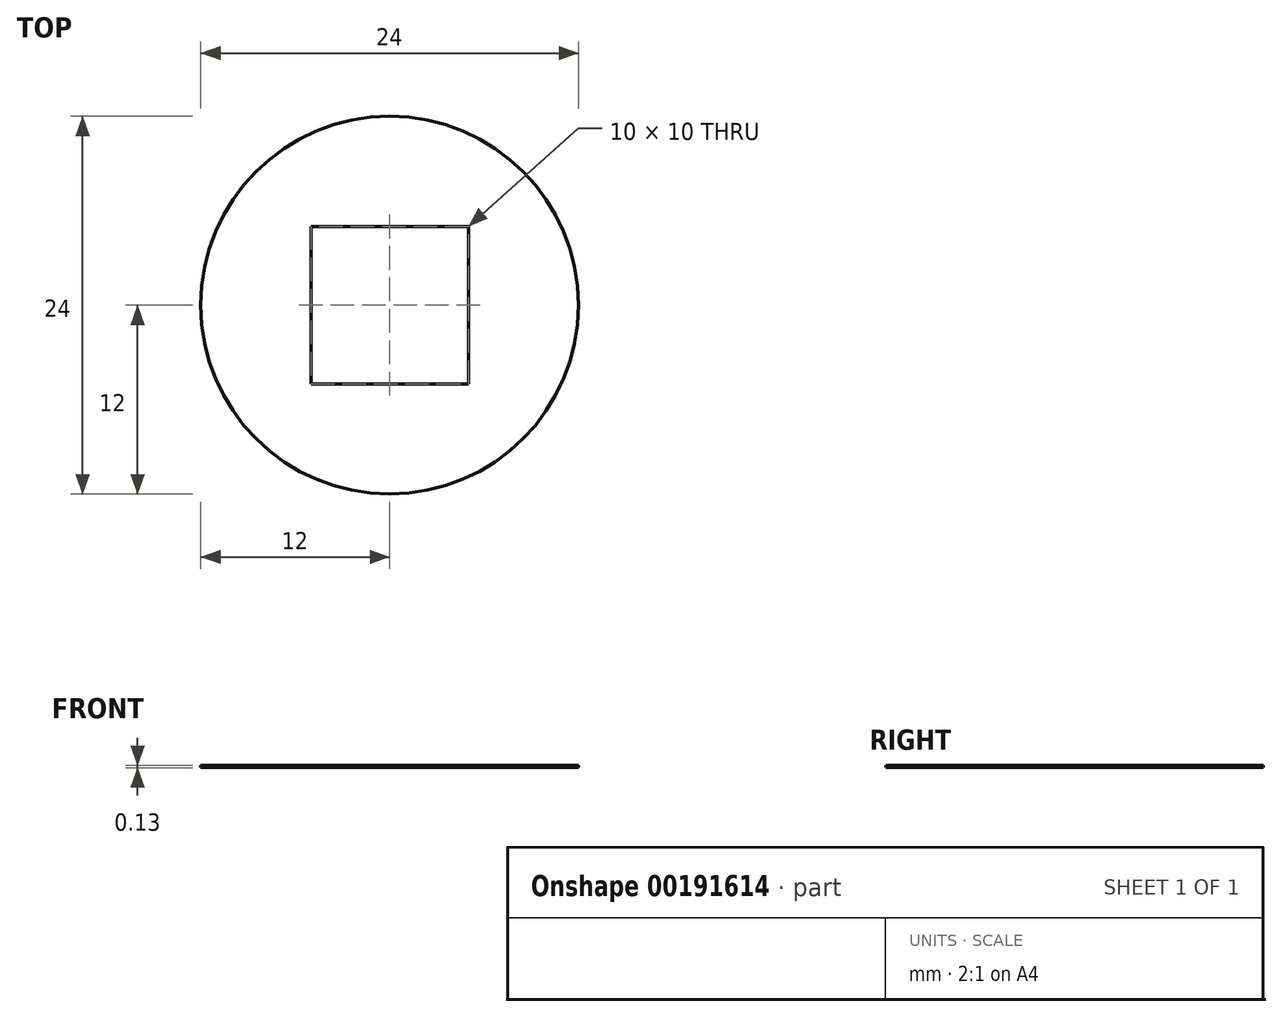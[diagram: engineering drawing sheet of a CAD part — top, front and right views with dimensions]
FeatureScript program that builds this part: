
annotation { "Feature Type Name" : "Feature", "Feature Type Description" : "" }
export const myFeature = defineFeature(function(context is Context, id is Id, definition is map)
    precondition{}
    {
        {
            var Q0;
            Q0=qCreatedBy(makeId("Top.planeOp"),FACE);
            var sketch = newSketch(context, id + "F0", { "sketchPlane" : qUnion([Q0])});
            skCircle(sketch, "E0", {"center": v(0, 0) * mm, "radius": 12 * mm});
            skSolve(sketch);
        }
        {
            var Q0;
            Q0 = qSketchRegion(id + "F0", true);
            extrude(context, id + "F1", {"entities" : qUnion([Q0]), "oppositeDirection" : true, "depth" : 0.12 * mm});
        }
        {
            var Q0;
            Q0=makeQuery(id+"F1.opExtrude","CAP_FACE",FACE,{"disambiguationData":[OSD([sQuery(id+"F0.wireOp",EDGE,"E0")])],"isStart":true});
            var sketch = newSketch(context, id + "F2", { "sketchPlane" : qUnion([Q0])});
            skLineSegment(sketch, "E1.bottom", {"start": v(5, 5) * mm, "end": v(-5, 5) * mm});
            skLineSegment(sketch, "E1.top", {"start": v(5, -5) * mm, "end": v(-5, -5) * mm});
            skLineSegment(sketch, "E1.left", {"start": v(5, 5) * mm, "end": v(5, -5) * mm});
            skLineSegment(sketch, "E1.right", {"start": v(-5, 5) * mm, "end": v(-5, -5) * mm});
            skPoint(sketch, "E1.middle", {"position": v(0, 0) * mm});
            skSolve(sketch);
        }
        {
            var Q0;
            Q0 = qSketchRegion(id + "F2", true);
            extrude(context, id + "F3", {"entities" : qUnion([Q0]), "operationType" : NewBodyOperationType.REMOVE, "endBound" : BoundingType.THROUGH_ALL, "oppositeDirection" : true, "depth" : 25.4 * mm});
        }
    });
